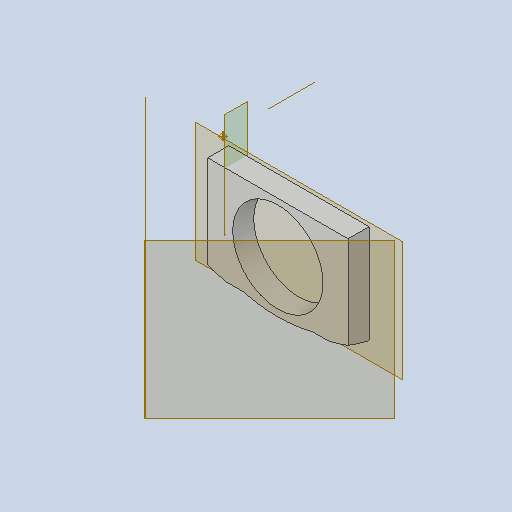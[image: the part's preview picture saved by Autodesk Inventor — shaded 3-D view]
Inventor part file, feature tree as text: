
AUTODESK INVENTOR PART (.ipt)
format: ipt  version: 2023 (Build 270158000, 158)  size: 211,456 bytes
history: native  units: in
note: dims shown in document units (in); Inventor stores cm internally (conversion verified against a paired STEP export)
features: reference x6, plane x5, other x5, sketch x4, extrude x4, projected_geometry x2, revolve x1, pattern_linear x1
ambient origin geometry x8: Origin, YZ Plane, XZ Plane, XY Plane, X Axis, Y Axis, Z Axis, Center Point
bodies: Solid1 (feature_tree)
feature tree (28):
  plane  "Work Plane1"
  sketch  "Sketch1"  dims[d0=1.5748in d1=1.063in]
  plane  "Work Plane2"
  extrude  "Extrusion1"  Depth=1.063in
  plane  "Work Plane3"
  revolve  "Revolution1"  Angle=90.0deg
  pattern_linear  "Rectangular Pattern1"  Count1=2  [1 undecoded]
  extrude  "Extrusion2"  Depth=0.3937in TaperAngle=0.0deg
  plane  "Work Plane4"
  extrude  "Extrusion3"  Depth=0.3937in TaperAngle=0.0deg
  plane  "Work Plane5"
  extrude  "Extrusion4"  Depth=0.3937in
  reference  "Reference1"
  reference  "Reference2"
  other  "Work Axis1"
  other  "Work Point1"
  sketch  "Sketch3"  dims[d3=0.3937in d4=0.0in d7=90.0deg d8=0.7874in d10=0.7874in d11=0.7874in d13=1.1811in]
  reference  "Reference3"
  reference  "Reference4"
  projected_geometry  "Projected Loop1"
  sketch  "Sketch4"  dims[d14=0.0394in d15=0.3937in d16=0.0in]
  reference  "Reference5"
  projected_geometry  "Projected Loop2"
  sketch  "Sketch5"  dims[d17=0.3937in d18=0.0in d19=0.3937in d20=0.0in d22=0.1929in d23=0.0591in d24=0.0591in d25=1.0118in]
  reference  "Reference6"
  other  "Assembly_Cube_Kinematic_Mirrormount_45_Thorlabs.iam"
  other  "20_Cube_Insert_Kinematic_Mirrormount_45_base:1"
  other  "00_PF10-03-P01-Step:1"
note: 1 required parameter value undecoded (feature->parameter linkage not recoverable at this tier; creation-order binding heuristic only, values carry confidence <= 0.55)
